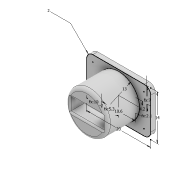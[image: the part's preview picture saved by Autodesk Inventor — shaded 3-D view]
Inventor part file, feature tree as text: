
AUTODESK INVENTOR PART (.ipt)
format: ipt  version: 2022 (Build 260153000, 153)  size: 200,704 bytes
history: native  units: mm
features: extrude x3, sketch x2, fillet x2
ambient origin geometry x8: Origin, YZ Plane, XZ Plane, XY Plane, X Axis, Y Axis, Z Axis, Center Point
bodies: Solid1 (feature_tree)
feature tree (7):
  sketch  "Sketch1"  dims[d0=10.6mm d1=4.2mm d2=2.1mm d3=5.3mm]
  extrude  "Extrusion1"  Depth=4.2mm
  fillet  "Fillet1"  Radius=2.1mm
  fillet  "Fillet2"  Radius=5.3mm
  extrude  "Extrusion2"  Depth=0.75mm
  extrude  "Extrusion3"  Depth=0.75mm
  sketch  "Sketch2"  dims[d4=13.0mm d5=20.0mm d6=14.0mm d7=10.0mm d8=7.0mm d9=2.0mm d10=10.0mm d11=0.0mm d12=0.5mm d13=1.0mm d14=1.5mm d15=0.0mm d16=0.75mm d17=0.0mm]
